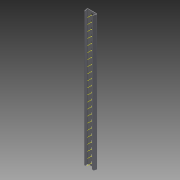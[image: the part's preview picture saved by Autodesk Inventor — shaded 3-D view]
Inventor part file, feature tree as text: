
AUTODESK INVENTOR PART (.ipt)
format: ipt  version: 2015 (Build 190159000, 159)  size: 434,688 bytes
history: native  units: in
note: dims shown in document units (in); Inventor stores cm internally (conversion verified against a paired STEP export)
features: other x25, boolean_combine x1, extrude x1, pattern_linear x1, plane x1, imported_body x1, sketch x1
ambient origin geometry x8: Origin, YZ Plane, XZ Plane, XY Plane, X Axis, Y Axis, Z Axis, Center Point
bodies: Body1 (feature_tree)
feature tree (31):
  boolean_combine  "Combine1"
  other  "Linear Slide"
  other  "Work Axis1"
  extrude  "Extrusion1"  TaperAngle=0.0deg  [1 undecoded]
  pattern_linear  "Rectangular Pattern1"  Spacing1=0.0in  [1 undecoded]
  plane  "Work Plane3"
  imported_body  "Base1"
  other  "Work Point1"
  other  "Work Axis2"
  sketch  "Sketch1"  dims[d0=8.6614in d2=0.5in d4=0.0in d5=0.0in d6=0.0in d9=-11.0in d10=0.0in]
  other  "Work Axis46"
  other  "Work Axis47"
  other  "Work Axis48"
  other  "Work Axis49"
  other  "Work Axis50"
  other  "Work Axis51"
  other  "Work Axis52"
  other  "Work Axis53"
  other  "Work Axis54"
  other  "Work Axis55"
  other  "Work Axis56"
  other  "Work Axis57"
  other  "Work Axis69"
  other  "Work Axis70"
  other  "Work Axis71"
  other  "Work Axis72"
  other  "Work Axis73"
  other  "Work Axis74"
  other  "Work Axis75"
  other  "Work Axis76"
  other  "bottom plane"
note: 2 required parameter values undecoded (feature->parameter linkage not recoverable at this tier; creation-order binding heuristic only, values carry confidence <= 0.55)
